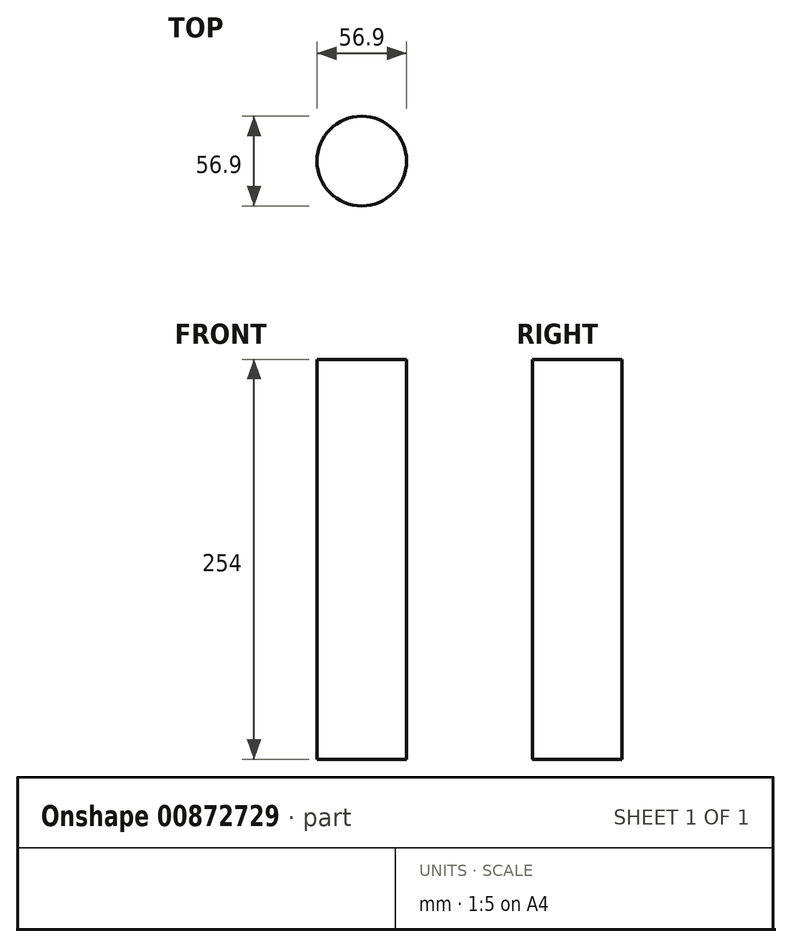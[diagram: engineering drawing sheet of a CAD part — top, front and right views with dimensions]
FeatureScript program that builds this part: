
annotation { "Feature Type Name" : "Feature", "Feature Type Description" : "" }
export const myFeature = defineFeature(function(context is Context, id is Id, definition is map)
    precondition{}
    {
        {
            var Q0;
            Q0=qCreatedBy(makeId("Top.planeOp"),FACE);
            var sketch = newSketch(context, id + "F0", { "sketchPlane" : qUnion([Q0])});
            skCircle(sketch, "E0", {"center": v(0, 0) * mm, "radius": 28.45 * mm});
            skSolve(sketch);
        }
        {
            var Q0;
            Q0 = qSketchRegion(id + "F0", true);
            extrude(context, id + "F1", {"entities" : qUnion([Q0]), "endBound" : BoundingType.SYMMETRIC, "depth" : 254 * mm, "offsetDistance" : 25.4 * mm});
        }
    });
